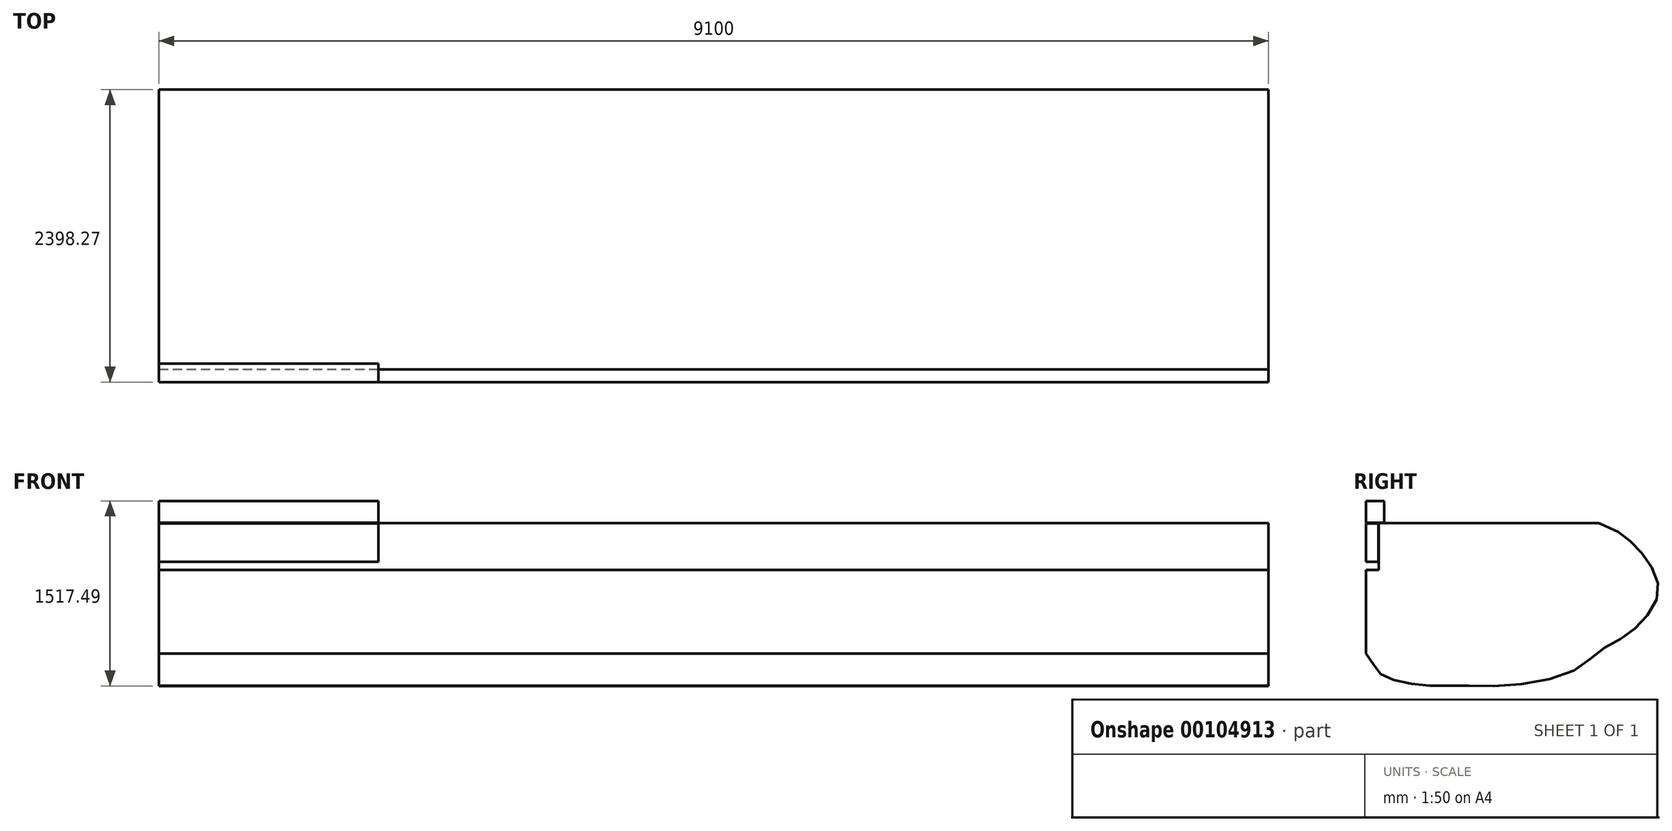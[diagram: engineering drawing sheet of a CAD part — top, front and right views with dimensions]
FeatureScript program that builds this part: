
annotation { "Feature Type Name" : "Feature", "Feature Type Description" : "" }
export const myFeature = defineFeature(function(context is Context, id is Id, definition is map)
    precondition{}
    {
        {
            var Q0;
            Q0=qCreatedBy(makeId("Right.planeOp"),FACE);
            var sketch = newSketch(context, id + "F0", { "sketchPlane" : qUnion([Q0])});
            skLineSegment(sketch, "E0.bottom", {"start": v(0, -289.12) * mm, "end": v(150, -289.12) * mm});
            skLineSegment(sketch, "E0.top", {"start": v(0, -469.12) * mm, "end": v(150, -469.12) * mm});
            skLineSegment(sketch, "E0.left", {"start": v(0, -289.12) * mm, "end": v(0, -469.12) * mm});
            skLineSegment(sketch, "E0.right", {"start": v(150, -289.12) * mm, "end": v(150, -469.12) * mm});
            skSolve(sketch);
        }
        {
            var Q0;
            Q0=qCreatedBy(makeId("Right.planeOp"),FACE);
            var sketch = newSketch(context, id + "F1", { "sketchPlane" : qUnion([Q0])});
            skLineSegment(sketch, "E1.top", {"start": v(0, -473.68) * mm, "end": v(101.53, -473.68) * mm});
            skLineSegment(sketch, "E1.left", {"start": v(0, -787.5) * mm, "end": v(0, -473.68) * mm});
            skLineSegment(sketch, "E1.right", {"start": v(101.53, -787.5) * mm, "end": v(101.53, -473.68) * mm});
            skLineSegment(sketch, "E2", {"start": v(0, -787.5) * mm, "end": v(101.53, -787.5) * mm});
            skSolve(sketch);
        }
        {
            var Q0;
            Q0=qSketchRegion(id+"F0",true);
            extrude(context, id + "F2", {"entities" : qUnion([Q0]), "depth" : 1800 * mm});
        }
        {
            var Q0;
            Q0=qSketchRegion(id+"F1",true);
            extrude(context, id + "F3", {"entities" : qUnion([Q0]), "depth" : 1800 * mm});
        }
        {
            var Q0;
            Q0=qCreatedBy(makeId("Right.planeOp"),FACE);
            var sketch = newSketch(context, id + "F4", { "sketchPlane" : qUnion([Q0])});
            skLineSegment(sketch, "E3.bottom", {"start": v(103.37, -470.76) * mm, "end": v(1892.88, -470.76) * mm});
            skLineSegment(sketch, "E3.left", {"start": v(103.37, -470.76) * mm, "end": v(103.37, -853.8) * mm});
            skLineSegment(sketch, "E4.left", {"start": v(0, -853.8) * mm, "end": v(0, -1540.58) * mm});
            skLineSegment(sketch, "E5", {"start": v(103.37, -853.8) * mm, "end": v(0, -853.8) * mm});
            skFitSpline(sketch, "E6", {"points": [v(1908.2, -470.76) * mm, v(2119.03, -580.72) * mm, v(2242.82, -693.9) * mm, v(2363.07, -874.27) * mm, v(2394.9, -1051.1) * mm, v(2288.8, -1252.7) * mm, v(2122.57, -1397.7) * mm, v(1920.98, -1517.94) * mm, v(1715.85, -1673.56) * mm, v(1221.99, -1797.79) * mm, v(775.49, -1804.08) * mm, v(527.09, -1804.08) * mm, v(284.97, -1772.63) * mm, v(130.9, -1716.03) * mm, v(71.16, -1646.86) * mm, v(0, -1540.58) * mm], "startDerivative": vector(4791.68, -1457.1) * mm, "endDerivative": vector(-1458.6, 2171.27) * mm});
            skArc(sketch, "E7.filletArc", {"start": v(1923.7, -475.63) * mm, "mid": v(1908.49, -471.98) * mm, "end": v(1892.88, -470.76) * mm});
            skSolve(sketch);
        }
        {
            var Q0;
            Q0=qSketchRegion(id+"F4",true);
            extrude(context, id + "F5", {"entities" : qUnion([Q0]), "depth" : 9100 * mm});
        }
    });
